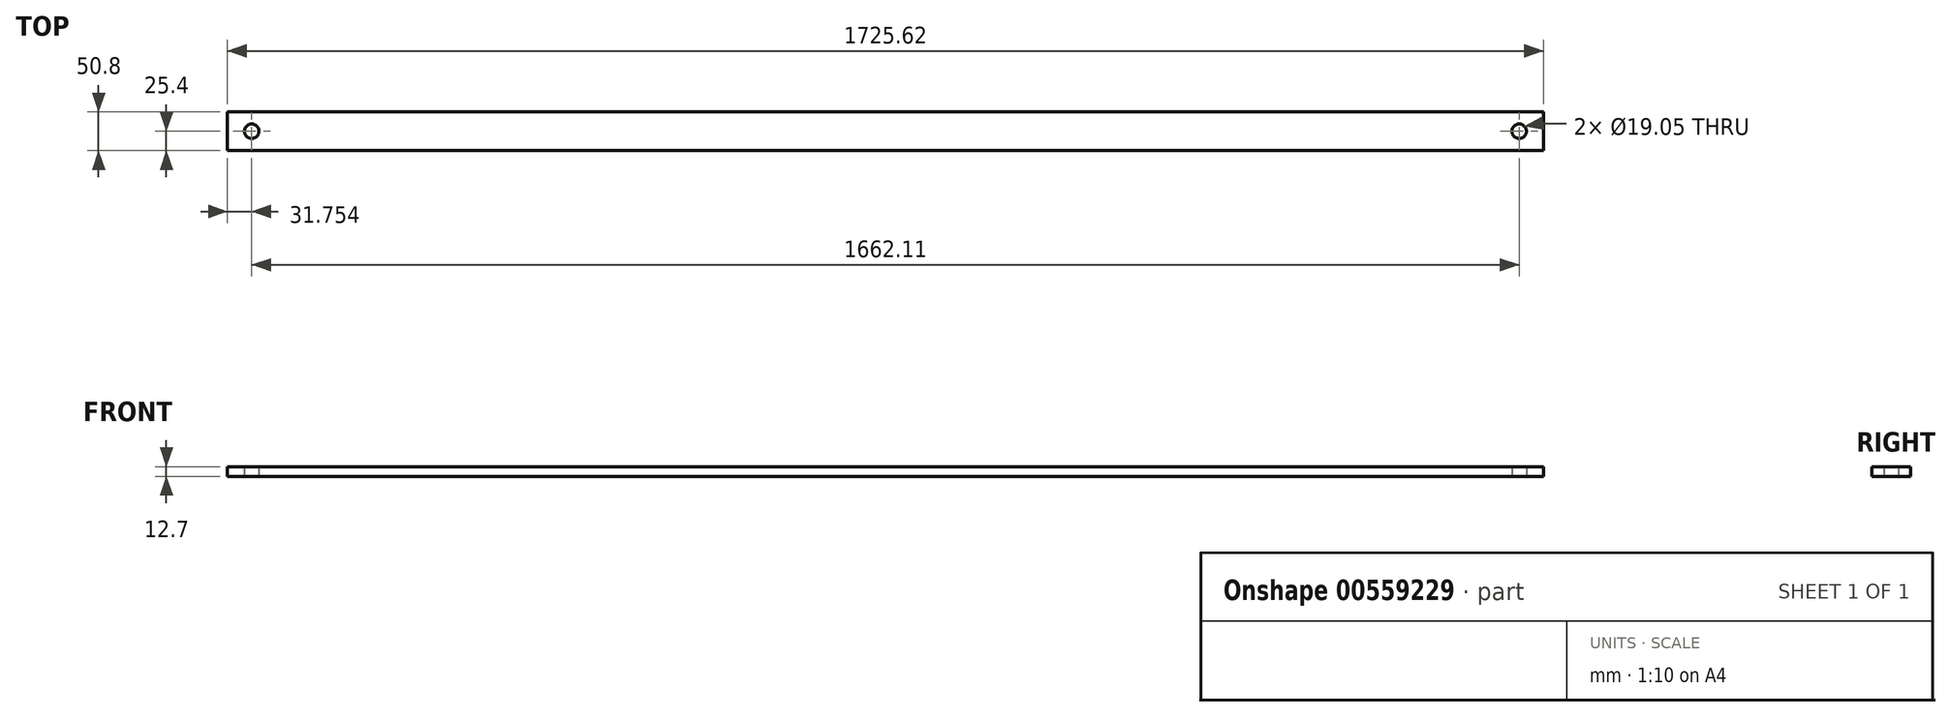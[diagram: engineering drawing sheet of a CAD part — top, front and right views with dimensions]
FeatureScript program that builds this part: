
annotation { "Feature Type Name" : "Feature", "Feature Type Description" : "" }
export const myFeature = defineFeature(function(context is Context, id is Id, definition is map)
    precondition{}
    {
        {
            var Q0;
            Q0=qCreatedBy(makeId("Top.planeOp"),FACE);
            var sketch = newSketch(context, id + "F0", { "sketchPlane" : qUnion([Q0])});
            skLineSegment(sketch, "E0.bottom", {"start": v(862.8, -25.4) * mm, "end": v(-862.8, -25.4) * mm});
            skLineSegment(sketch, "E0.top", {"start": v(862.8, 25.4) * mm, "end": v(-862.8, 25.4) * mm});
            skLineSegment(sketch, "E0.left", {"start": v(862.8, -25.4) * mm, "end": v(862.8, 25.4) * mm});
            skLineSegment(sketch, "E0.right", {"start": v(-862.8, -25.4) * mm, "end": v(-862.8, 25.4) * mm});
            skPoint(sketch, "E0.middle", {"position": v(0, 0) * mm});
            skSolve(sketch);
        }
        {
            var Q0;
            Q0 = qSketchRegion(id + "F0", true);
            extrude(context, id + "F1", {"entities" : qUnion([Q0]), "depth" : 12.7 * mm, "offsetDistance" : 25.4 * mm});
        }
        {
            var Q0;
            Q0=makeQuery(id+"F1.opExtrude","CAP_FACE",FACE,{"disambiguationData":[OSD([sQuery(id+"F0.wireOp",EDGE,"E0.bottom"),sQuery(id+"F0.wireOp",EDGE,"E0.top"),sQuery(id+"F0.wireOp",EDGE,"E0.left"),sQuery(id+"F0.wireOp",EDGE,"E0.right")])],"isStart":true});
            var sketch = newSketch(context, id + "F2", { "sketchPlane" : qUnion([Q0])});
            skCircle(sketch, "E1", {"center": v(-831.06, 0) * mm, "radius": 9.53 * mm});
            skCircle(sketch, "E2.MirrorC", {"center": v(831.06, 0) * mm, "radius": 9.53 * mm});
            skSolve(sketch);
        }
        {
            var Q0;
            Q0 = qSketchRegion(id + "F2", true);
            extrude(context, id + "F3", {"entities" : qUnion([Q0]), "operationType" : NewBodyOperationType.REMOVE, "oppositeDirection" : true, "depth" : 25.4 * mm, "offsetDistance" : 25.4 * mm});
        }
    });
